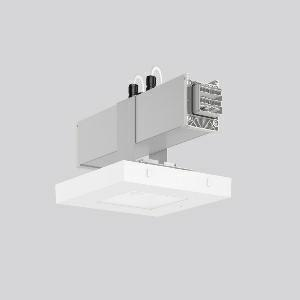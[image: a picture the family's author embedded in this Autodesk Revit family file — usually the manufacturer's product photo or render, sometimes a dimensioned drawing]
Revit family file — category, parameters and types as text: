
# Revit family: linedo_module_rf_9503rf_760_430_000_5822
name_source: partatom
category: Lighting Fixtures
units: mm (PartAtom-declared; Revit-internal decimal feet)

## family parameters
Cut with Voids When Loaded = No
Host = Face
Light Source = No
Part Type = Normal
Room Calculation Point = No
Round Connector Dimension = Use Diameter
Shared = No

## types (1)
- LINEDO Module RF (1 x LED Modul 765, 390 lm, 6500)
    Apparent Load = 7 VA
    CIE Flux Codes = 49 90 100 100 100
    Color Rendering = 70
    Color Temperature = 6500
    Default Elevation = 1800 mm
    Description = LINEDO, 6,7 W, 390 lm, 765, silver, on/off
Continuous line luminaire, L 330 B 198 H 170, SBS, 3 h, emergency-310 lm, automatischer Selbsttest
    Height = 170 mm  [stored 0.557743 ft]
    Lamp = 1 x LED Modul 765
    Lamp Light Flux = 390 lm
    Lamp count = 1
    Length = 330 mm
    Lifetime = 50000 h
    Luminous efficacy = 58 lm/W
    Manufacturer = RZB
    ModVariant = No
    Model = 9503RF.760.430.000
    Mounting Place = Ceiling
    Mounting Type = Surface mounted, Pendant
    Number of Poles = 1
    OnlyDefault = Yes
    Power Factor = 1
    Product Name = LINEDO Module RF
    Product group = Continuous line luminaire system Linedo IP 54
    ProductGroupID = 314
    Protection Class = Protection class I
    Protection Degree = IP 54
    RLX_Detail_Level = 1
    RLX_Emergency_Light_Flux = 310 lm
    RLX_Emergency_Type = 3
    RLX_Emergency_Type_DB = Yes
    RlxData = <blob elided: 22125 chars, md5=0bdde52f>
    Socket = socket
    Standby Power = 0 W
    System Light Flux = 390 lm
    System Power = 7 W
    Type Comments = Product without accessories
    Type Image = 9503rw.760.434.000.jpg
    URL = http://relux.com
    VarID = ---
    Voltage = 230 V
    Voltage Range = 220-240 V
    Weight = 0.00 kg
    Width = 198 mm

note: [stored X ft] marks values corroborated as IEEE doubles in the binary element streams (Revit-internal decimal feet)

## geometry (parser evidence)
native form markers: Blend x4, Sweep x13
no freeform markers — native parametric forms only
